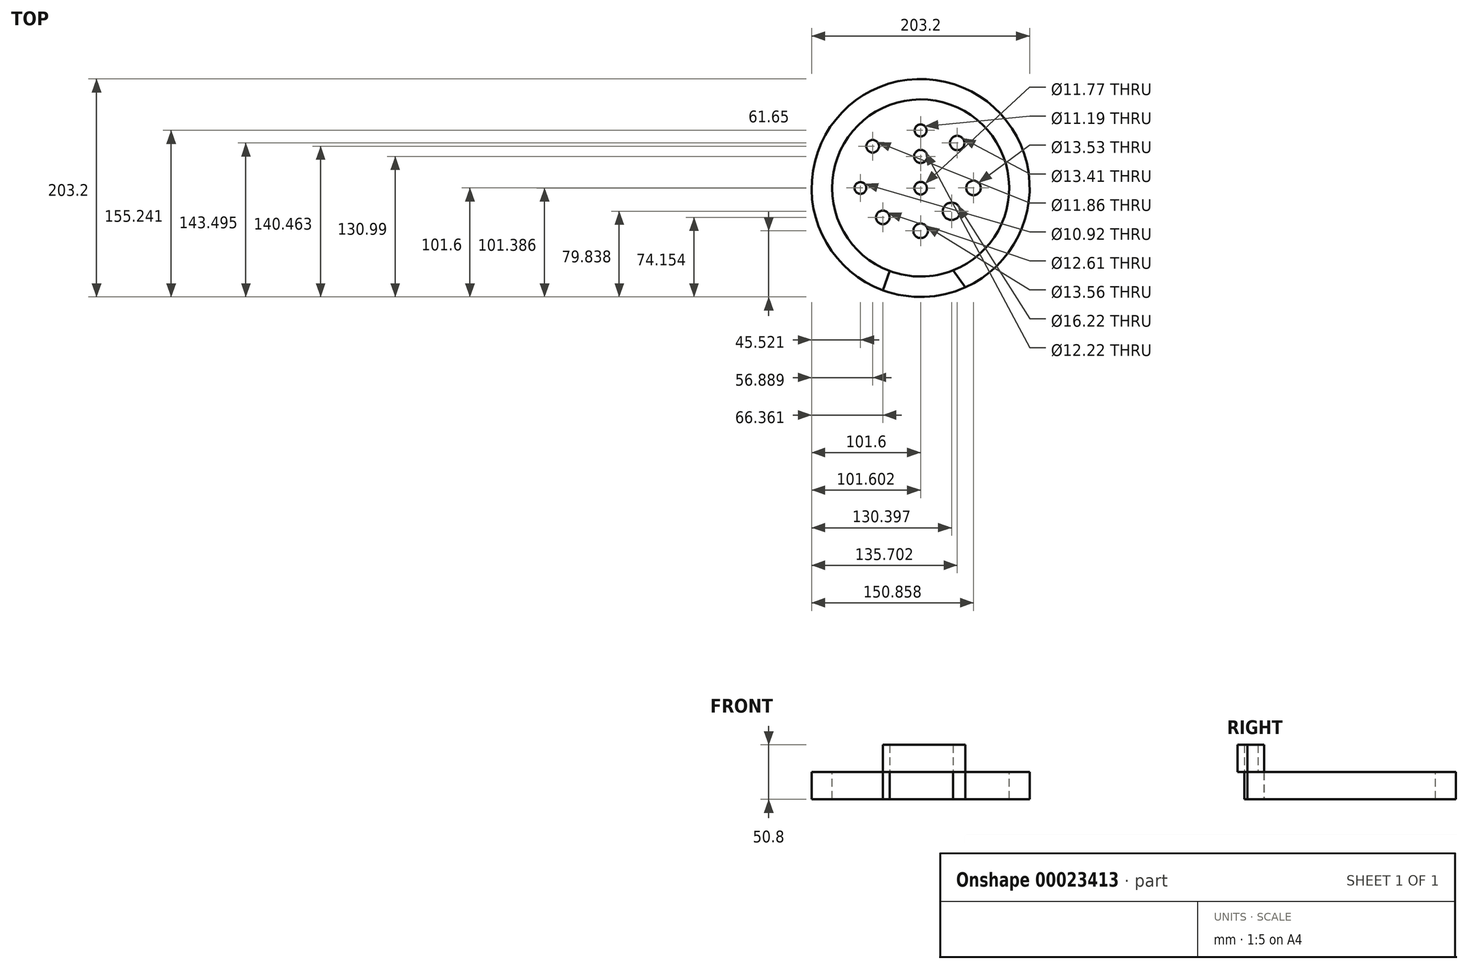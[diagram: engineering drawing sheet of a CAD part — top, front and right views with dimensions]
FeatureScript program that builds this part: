
annotation { "Feature Type Name" : "Feature", "Feature Type Description" : "" }
export const myFeature = defineFeature(function(context is Context, id is Id, definition is map)
    precondition{}
    {
        {
            var Q0;
            Q0=qCreatedBy(makeId("Top.planeOp"),FACE);
            var sketch = newSketch(context, id + "F0", { "sketchPlane" : qUnion([Q0])});
            skCircle(sketch, "E0", {"center": v(0, 0) * mm, "radius": 101.6 * mm});
            skCircle(sketch, "E1", {"center": v(0, 0) * mm, "radius": 82.55 * mm});
            skArc(sketch, "E2", {"start": v(-28.88, -77.33) * mm, "mid": v(0.68, -82.56) * mm, "end": v(30.15, -76.85) * mm});
            skArc(sketch, "E3", {"start": v(-35.09, -95.35) * mm, "mid": v(3.5, -101.9) * mm, "end": v(41.56, -92.71) * mm});
            skLineSegment(sketch, "E4", {"start": v(-28.88, -77.33) * mm, "end": v(-35.09, -95.35) * mm});
            skLineSegment(sketch, "E5", {"start": v(30.15, -76.85) * mm, "end": v(41.56, -92.71) * mm});
            skCircle(sketch, "E6", {"center": v(0, -0.21) * mm, "radius": 5.89 * mm});
            skCircle(sketch, "E7", {"center": v(0, 53.64) * mm, "radius": 5.6 * mm});
            skCircle(sketch, "E8", {"center": v(49.26, 0) * mm, "radius": 6.76 * mm});
            skCircle(sketch, "E9", {"center": v(34.1, 41.9) * mm, "radius": 6.7 * mm});
            skCircle(sketch, "E10", {"center": v(-44.71, 38.86) * mm, "radius": 5.93 * mm});
            skCircle(sketch, "E11", {"center": v(-56.08, 0) * mm, "radius": 5.46 * mm});
            skCircle(sketch, "E12", {"center": v(-35.24, -27.45) * mm, "radius": 6.3 * mm});
            skCircle(sketch, "E13", {"center": v(0, -39.95) * mm, "radius": 6.78 * mm});
            skCircle(sketch, "E14", {"center": v(28.8, -21.76) * mm, "radius": 8.1 * mm});
            skCircle(sketch, "E15", {"center": v(0, 29.4) * mm, "radius": 6.1 * mm});
            skSolve(sketch);
        }
        {
            var Q0;
            {var subQ0=sQuery(id+"F0.wireOp",EDGE,"E1");var subQ1=sQuery(id+"F0.wireOp",EDGE,"E2");var subQ3=makeQuery(id+"F0.imprint","INTERSECT",VERTEX,{"derivedFrom":[subQ0,subQ1,sQuery(id+"F0.wireOp",EDGE,"E4")]});Q0=makeQuery(id+"F0.imprint","IMPRINT",FACE,{"disambiguationData":[TD([[makeQuery(id+"F0.imprint","IMPRINT",EDGE,{"disambiguationData":[TD([[subQ3,-1.0]])],"derivedFrom":subQ0}),1.0]])]});}
            extrude(context, id + "F1", {"entities" : qUnion([Q0]), "depth" : 0.25 * mm});
        }
        {
            var Q0;
            Q0=makeQuery(id+"F0.imprint","IMPRINT",FACE,{"disambiguationData":[TD([[makeQuery(id+"F0.imprint","IMPRINT",EDGE,{"derivedFrom":sQuery(id+"F0.wireOp",EDGE,"E2")}),-1.0]])]});
            extrude(context, id + "F2", {"entities" : qUnion([Q0]), "depth" : 50.8 * mm});
        }
        {
            var Q0;
            Q0=makeQuery(id+"F0.imprint","IMPRINT",FACE,{"disambiguationData":[TD([[makeQuery(id+"F0.imprint","IMPRINT",EDGE,{"derivedFrom":sQuery(id+"F0.wireOp",EDGE,"E2")}),-1.0]])]});
            extrude(context, id + "F3", {"entities" : qUnion([Q0]), "operationType" : NewBodyOperationType.REMOVE, "depth" : 25.4 * mm});
        }
        {
            var Q0;
            Q0=makeQuery(id+"F1.opExtrude","CAP_FACE",FACE,{"disambiguationData":[OSD([sQuery(id+"F0.wireOp",EDGE,"E1")])],"isStart":false});
            var Q1;
            {var subQ1=sQuery(id+"F0.wireOp",EDGE,"E4");Q1=makeQuery(id+"F0.imprint","IMPRINT",FACE,{"disambiguationData":[TD([[makeQuery(id+"F0.imprint","IMPRINT",EDGE,{"derivedFrom":subQ1}),-1.0]])]});}
            extrude(context, id + "F4", {"entities" : qUnion([Q0, Q1]), "operationType" : NewBodyOperationType.ADD, "depth" : 25.4 * mm});
        }
        {
            var Q0;
            Q0=makeQuery(id+"F4.opExtrude","CAP_FACE",FACE,{"disambiguationData":[OSD([sQuery(id+"F0.wireOp",EDGE,"E1"),sQuery(id+"F0.wireOp",EDGE,"E6"),sQuery(id+"F0.wireOp",EDGE,"E7"),sQuery(id+"F0.wireOp",EDGE,"E8"),sQuery(id+"F0.wireOp",EDGE,"E9"),sQuery(id+"F0.wireOp",EDGE,"E10"),sQuery(id+"F0.wireOp",EDGE,"E11"),sQuery(id+"F0.wireOp",EDGE,"E12"),sQuery(id+"F0.wireOp",EDGE,"E13"),sQuery(id+"F0.wireOp",EDGE,"E14"),sQuery(id+"F0.wireOp",EDGE,"E15")])],"isStart":false});
            extrude(context, id + "F5", {"entities" : qUnion([Q0]), "operationType" : NewBodyOperationType.REMOVE, "oppositeDirection" : true, "depth" : 25.4 * mm});
        }
    });
